FCSTD DOCUMENT  (FreeCAD 1.0R39109 (Git))
Label: XY-Assembly
License: All rights reserved
LicenseURL: https://en.wikipedia.org/wiki/All_rights_reserved
objects: App::FeaturePython×23, App::Link×20, Assembly::AssemblyLink×6, Assembly::JointGroup×1, Assembly::AssemblyObject×1
EXTERNAL_REF file=../Profiles/20x20-I-Type-356mm.FCStd obj=Fusion001
EXTERNAL_REF file=../LinearGuides/MGN12-Rail-300mm.FCStd obj=Part__Feature
EXTERNAL_REF file=SingleCrossCarriageAssembly.FCStd obj=Assembly
EXTERNAL_REF file=SingleCrossCarriageAssembly.FCStd obj=Assembly001
EXTERNAL_REF file=CarriageLinearGuideAssembly.FCStd obj=Body
EXTERNAL_REF file=CarriageLinearGuideAssembly.FCStd obj=Vagon_MGN_021
EXTERNAL_REF file=SingleCrossCarriageAssembly.FCStd obj=Assembly002
EXTERNAL_REF file=SingleCrossCarriageAssembly.FCStd obj=Cube
EXTERNAL_REF file=SingleCrossCarriageAssembly.FCStd obj=Body002

FEATURE [App::Link] Profile_20x20_I_Type_Slot5  label="Profile-20x20-I-Type_Slot5"
  LinkPlacement = pos=(0,-178,178) rot=(1,0,0;4.71239rad)
  LinkedObject = -> <external ../Profiles/20x20-I-Type-356mm.FCStd>#Fusion001
  Placement = pos=(0,-178,178) rot=(1,0,0;4.71239rad)
FEATURE [App::FeaturePython] GroundedJoint  # Assembly grounded joint (typed FeaturePython)
  ObjectToGround = -> Profile_20x20_I_Type_Slot5
  Placement = pos=(0,-178,178) rot=(1,0,0;4.71239rad)
FEATURE [App::Link] Profile_20x20_I_Type_Slot006  label="Profile-20x20-I-Type_Slot006"
  LinkPlacement = pos=(10,-188,180.494) rot=(0,1,0;1.5708rad)
  LinkedObject = -> <external ../Profiles/20x20-I-Type-356mm.FCStd>#Fusion001
  Placement = pos=(10,-188,180.494) rot=(0,1,0;1.5708rad)
FEATURE [App::Link] Profile_20x20_I_Type_Slot007  label="Profile-20x20-I-Type_Slot007"
  LinkPlacement = pos=(10,188,180.494) rot=(0,1,0;1.5708rad)
  LinkedObject = -> <external ../Profiles/20x20-I-Type-356mm.FCStd>#Fusion001
  Placement = pos=(10,188,180.494) rot=(0,1,0;1.5708rad)
FEATURE [App::Link] Profile_20x20_I_Type_Slot008  label="Profile-20x20-I-Type_Slot008"
  LinkPlacement = pos=(376,178,178) rot=(-0.57735,-0.57735,0.57735;4.18879rad)
  LinkedObject = -> <external ../Profiles/20x20-I-Type-356mm.FCStd>#Fusion001
  Placement = pos=(376,178,178) rot=(-0.57735,-0.57735,0.57735;4.18879rad)
FEATURE [App::FeaturePython] Joint  label="Distance"  # Assembly joint (typed FeaturePython)
  Activated = true
  AngleMax = 0
  AngleMin = 0
  Detach1 = false
  Detach2 = false
  Distance = 0
  Distance2 = 0
  EnableAngleMax = false
  EnableAngleMin = false
  EnableLengthMax = false
  EnableLengthMin = false
  JointType = 5 (Distance)
  LengthMax = 0
  LengthMin = 0
  Placement1 = pos=(-5.81322,5.81322,0) rot=(0,0,1;0rad)
  Placement2 = pos=(10,-5.97447,178) rot=(0.57735,0.57735,-0.57735;4.18879rad)
  Reference1 = -> Assembly [Profile_20x20_I_Type_Slot006.Face33,Profile_20x20_I_Type_Slot006.Edge18]
  Reference2 = -> Assembly [Profile_20x20_I_Type_Slot5.Face21,Profile_20x20_I_Type_Slot5.Face21]
FEATURE [App::FeaturePython] Joint001  label="Distance001"  # Assembly joint (typed FeaturePython)
  Activated = true
  AngleMax = 0
  AngleMin = 0
  Detach1 = false
  Detach2 = false
  Distance = 0
  Distance2 = 0
  EnableAngleMax = false
  EnableAngleMin = false
  EnableLengthMax = false
  EnableLengthMin = false
  JointType = 5 (Distance)
  LengthMax = 0
  LengthMin = 0
  Placement1 = pos=(-5.81322,-5.81322,0) rot=(-1,0,0;3.14159rad)
  Placement2 = pos=(-5.97447,10,178) rot=(-1,0,0;1.5708rad)
  Reference1 = -> Assembly [Profile_20x20_I_Type_Slot5.Face10,Profile_20x20_I_Type_Slot5.Edge18]
  Reference2 = -> Assembly [Profile_20x20_I_Type_Slot006.Face85,Profile_20x20_I_Type_Slot006.Vertex140]
FEATURE [App::FeaturePython] Joint002  label="Distance002"  # Assembly joint (typed FeaturePython)
  Activated = true
  AngleMax = 0
  AngleMin = 0
  Detach1 = false
  Detach2 = false
  Distance = 0
  Distance2 = 0
  EnableAngleMax = false
  EnableAngleMin = false
  EnableLengthMax = false
  EnableLengthMin = false
  JointType = 5 (Distance)
  LengthMax = 0
  LengthMin = 0
  Placement1 = pos=(10,-5.97447,178) rot=(0.57735,0.57735,-0.57735;4.18879rad)
  Placement2 = pos=(-5.81322,-5.81322,0) rot=(1,0,0;3.14159rad)
  Reference1 = -> Assembly [Profile_20x20_I_Type_Slot5.Face21,Profile_20x20_I_Type_Slot5.Vertex41]
  Reference2 = -> Assembly [Profile_20x20_I_Type_Slot007.Face10,Profile_20x20_I_Type_Slot007.Vertex61]
FEATURE [App::FeaturePython] Joint003  label="Distance003"  # Assembly joint (typed FeaturePython)
  Activated = true
  AngleMax = 0
  AngleMin = 0
  Detach1 = false
  Detach2 = false
  Distance = 0
  Distance2 = 0
  EnableAngleMax = false
  EnableAngleMin = false
  EnableLengthMax = false
  EnableLengthMin = false
  JointType = 5 (Distance)
  LengthMax = 0
  LengthMin = 0
  Placement1 = pos=(5.81322,-5.81322,356) rot=(0,0,-1;3.14159rad)
  Placement2 = pos=(-5.97447,-10,178) rot=(-1,0,0;1.5708rad)
  Reference1 = -> Assembly [Profile_20x20_I_Type_Slot5.Face5,Profile_20x20_I_Type_Slot5.Edge18]
  Reference2 = -> Assembly [Profile_20x20_I_Type_Slot007.Face44,Profile_20x20_I_Type_Slot007.Vertex61]
FEATURE [App::FeaturePython] Joint004  label="Distance004"  # Assembly joint (typed FeaturePython)
  Activated = true
  AngleMax = 0
  AngleMin = 0
  Detach1 = false
  Detach2 = false
  Distance = 0
  Distance2 = 0
  EnableAngleMax = false
  EnableAngleMin = false
  EnableLengthMax = false
  EnableLengthMin = false
  JointType = 5 (Distance)
  LengthMax = 0
  LengthMin = 0
  Placement1 = pos=(-5.97447,10,178) rot=(-1,0,0;1.5708rad)
  Placement2 = pos=(-5.81322,-5.81322,356) rot=(1,0,0;3.14159rad)
  Reference1 = -> Assembly [Profile_20x20_I_Type_Slot006.Face85,Profile_20x20_I_Type_Slot006.Vertex157]
  Reference2 = -> Assembly [Profile_20x20_I_Type_Slot008.Face25,Profile_20x20_I_Type_Slot008.Edge18]
FEATURE [App::FeaturePython] Joint005  label="Distance005"  # Assembly joint (typed FeaturePython)
  Activated = true
  AngleMax = 0
  AngleMin = 0
  Detach1 = false
  Detach2 = false
  Distance = 0
  Distance2 = 0
  EnableAngleMax = false
  EnableAngleMin = false
  EnableLengthMax = false
  EnableLengthMin = false
  JointType = 5 (Distance)
  LengthMax = 0
  LengthMin = 0
  Placement1 = pos=(-5.81322,5.81322,356) rot=(0,0,1;0rad)
  Placement2 = pos=(-5.97447,-10,178) rot=(-1,0,0;1.5708rad)
  Reference1 = -> Assembly [Profile_20x20_I_Type_Slot006.Face68,Profile_20x20_I_Type_Slot006.Vertex151]
  Reference2 = -> Assembly [Profile_20x20_I_Type_Slot008.Face44,Profile_20x20_I_Type_Slot008.Vertex101]
FEATURE [App::FeaturePython] Joint006  label="Distance006"  # Assembly joint (typed FeaturePython)
  Activated = true
  AngleMax = 0
  AngleMin = 0
  Detach1 = false
  Detach2 = false
  Distance = 0
  Distance2 = 0
  EnableAngleMax = false
  EnableAngleMin = false
  EnableLengthMax = false
  EnableLengthMin = false
  JointType = 5 (Distance)
  LengthMax = 0
  LengthMin = 0
  Placement1 = pos=(5.97447,-10,178) rot=(0,0.707107,-0.707107;3.14159rad)
  Placement2 = pos=(-10,-5.97447,178) rot=(-0.57735,-0.57735,0.57735;2.0944rad)
  Reference1 = -> Assembly [Profile_20x20_I_Type_Slot5.Face23,Profile_20x20_I_Type_Slot5.Vertex43]
  Reference2 = -> Assembly [Profile_20x20_I_Type_Slot008.Face42,Profile_20x20_I_Type_Slot008.Face42]
FEATURE [App::FeaturePython] Joint007  label="Distance007"  # Assembly joint (typed FeaturePython)
  Activated = true
  AngleMax = 0
  AngleMin = 0
  Detach1 = false
  Detach2 = false
  Distance = 0
  Distance2 = 0
  EnableAngleMax = false
  EnableAngleMin = false
  EnableLengthMax = false
  EnableLengthMin = false
  JointType = 5 (Distance)
  LengthMax = 0
  LengthMin = 0
  Placement1 = pos=(-10,-5.97447,178) rot=(-0.57735,-0.57735,0.57735;2.0944rad)
  Placement2 = pos=(-10,5.97447,178) rot=(-0.57735,0.57735,-0.57735;2.0944rad)
  Reference1 = -> Assembly [Profile_20x20_I_Type_Slot007.Face42,Profile_20x20_I_Type_Slot007.Face42]
  Reference2 = -> Assembly [Profile_20x20_I_Type_Slot006.Face83,Profile_20x20_I_Type_Slot006.Face83]
FEATURE [App::Link] Rail_12  label="Rail 12"
  LinkPlacement = pos=(13.95,-150,178) rot=(0,-1,0;1.5708rad)
  LinkedObject = -> <external ../LinearGuides/MGN12-Rail-300mm.FCStd>#Part__Feature
  Placement = pos=(13.95,-150,178) rot=(0,-1,0;1.5708rad)
FEATURE [App::Link] Rail_013  label="Rail 013"
  LinkPlacement = pos=(362.05,150,178) rot=(0.707107,0,0.707107;3.14159rad)
  LinkedObject = -> <external ../LinearGuides/MGN12-Rail-300mm.FCStd>#Part__Feature
  Placement = pos=(362.05,150,178) rot=(0.707107,0,0.707107;3.14159rad)
FEATURE [App::Link] Rail_014  label="Rail 014"
  LinkPlacement = pos=(338,-174.05,180.494) rot=(0.57735,-0.57735,0.57735;2.0944rad)
  LinkedObject = -> <external ../LinearGuides/MGN12-Rail-300mm.FCStd>#Part__Feature
  Placement = pos=(338,-174.05,180.494) rot=(0.57735,-0.57735,0.57735;2.0944rad)
FEATURE [App::Link] Rail_015  label="Rail 015"
  LinkPlacement = pos=(38,174.05,180.494) rot=(0.57735,0.57735,0.57735;4.18879rad)
  LinkedObject = -> <external ../LinearGuides/MGN12-Rail-300mm.FCStd>#Part__Feature
  Placement = pos=(38,174.05,180.494) rot=(0.57735,0.57735,0.57735;4.18879rad)
FEATURE [App::FeaturePython] Joint008  label="Distance008"  # Assembly joint (typed FeaturePython)
  Activated = true
  AngleMax = 0
  AngleMin = 0
  Detach1 = false
  Detach2 = false
  Distance = 0
  Distance2 = 0
  EnableAngleMax = false
  EnableAngleMin = false
  EnableLengthMax = false
  EnableLengthMin = false
  JointType = 5 (Distance)
  LengthMax = 0
  LengthMin = 0
  Placement1 = pos=(1.30928,149.976,3.95) rot=(0,1,0;3.14159rad)
  Placement2 = pos=(10,-5.97447,178) rot=(0.57735,0.57735,-0.57735;4.18879rad)
  Reference1 = -> Assembly [Rail_12.Face37,Rail_12.Vertex52]
  Reference2 = -> Assembly [Profile_20x20_I_Type_Slot5.Face21,Profile_20x20_I_Type_Slot5.Vertex23]
FEATURE [App::FeaturePython] Joint009  label="Distance009"  # Assembly joint (typed FeaturePython)
  Activated = true
  AngleMax = 0
  AngleMin = 0
  Detach1 = false
  Detach2 = false
  Distance = 0
  Distance2 = 0
  EnableAngleMax = false
  EnableAngleMin = false
  EnableLengthMax = false
  EnableLengthMin = false
  JointType = 5 (Distance)
  LengthMax = 0
  LengthMin = 0
  Placement1 = pos=(1.30928,149.976,3.95) rot=(0,-1,0;3.14159rad)
  Placement2 = pos=(-5.97447,-10,178) rot=(-1,0,0;1.5708rad)
  Reference1 = -> Assembly [Rail_013.Face37,Rail_013.Vertex64]
  Reference2 = -> Assembly [Profile_20x20_I_Type_Slot008.Face44,Profile_20x20_I_Type_Slot008.Face44]
FEATURE [App::FeaturePython] Joint010  label="Distance010"  # Assembly joint (typed FeaturePython)
  Activated = true
  AngleMax = 0
  AngleMin = 0
  Detach1 = false
  Detach2 = false
  Distance = 0
  Distance2 = 0
  EnableAngleMax = false
  EnableAngleMin = false
  EnableLengthMax = false
  EnableLengthMin = false
  JointType = 5 (Distance)
  LengthMax = 0
  LengthMin = 0
  Placement1 = pos=(1.30928,149.976,3.95) rot=(0,-1,0;3.14159rad)
  Placement2 = pos=(-5.97447,-10,178) rot=(-1,0,0;1.5708rad)
  Reference1 = -> Assembly [Rail_015.Face37,Rail_015.Edge19]
  Reference2 = -> Assembly [Profile_20x20_I_Type_Slot007.Face44,Profile_20x20_I_Type_Slot007.Face44]
FEATURE [App::FeaturePython] Joint011  label="Distance011"  # Assembly joint (typed FeaturePython)
  Activated = true
  AngleMax = 0
  AngleMin = 0
  Detach1 = false
  Detach2 = false
  Distance = 0
  Distance2 = 0
  EnableAngleMax = false
  EnableAngleMin = false
  EnableLengthMax = false
  EnableLengthMin = false
  JointType = 5 (Distance)
  LengthMax = 0
  LengthMin = 0
  Placement1 = pos=(1.30928,149.976,3.95) rot=(0,-1,0;3.14159rad)
  Placement2 = pos=(-5.97447,10,178) rot=(-1,0,0;1.5708rad)
  Reference1 = -> Assembly [Rail_014.Face37,Rail_014.Edge17]
  Reference2 = -> Assembly [Profile_20x20_I_Type_Slot006.Face85,Profile_20x20_I_Type_Slot006.Vertex157]
FEATURE [App::FeaturePython] Joint012  label="Distance012"  # Assembly joint (typed FeaturePython)
  Activated = true
  AngleMax = 0
  AngleMin = 0
  Detach1 = false
  Detach2 = false
  Distance = -4
  Distance2 = 0
  EnableAngleMax = false
  EnableAngleMin = false
  EnableLengthMax = false
  EnableLengthMin = false
  JointType = 5 (Distance)
  LengthMax = 0
  LengthMin = 0
  Placement1 = pos=(-10,-5.97447,178) rot=(-0.57735,-0.57735,0.57735;2.0944rad)
  Placement2 = pos=(6,150,1.25) rot=(0,-1,0;1.5708rad)
  Reference1 = -> Assembly [Profile_20x20_I_Type_Slot008.Face42,Profile_20x20_I_Type_Slot008.Face42]
  Reference2 = -> Assembly [Rail_013.Face49,Rail_013.Face49]
FEATURE [App::FeaturePython] Joint013  label="Distance013"  # Assembly joint (typed FeaturePython)
  Activated = true
  AngleMax = 0
  AngleMin = 0
  Detach1 = false
  Detach2 = false
  Distance = -4
  Distance2 = 0
  EnableAngleMax = false
  EnableAngleMin = false
  EnableLengthMax = false
  EnableLengthMin = false
  JointType = 5 (Distance)
  LengthMax = 0
  LengthMin = 0
  Placement1 = pos=(6,150,1.25) rot=(0,-1,0;1.5708rad)
  Placement2 = pos=(-10,-5.97447,178) rot=(-0.57735,-0.57735,0.57735;2.0944rad)
  Reference1 = -> Assembly [Rail_015.Face49,Rail_015.Face49]
  Reference2 = -> Assembly [Profile_20x20_I_Type_Slot007.Face42,Profile_20x20_I_Type_Slot007.Face42]
FEATURE [App::FeaturePython] Joint014  label="Distance014"  # Assembly joint (typed FeaturePython)
  Activated = true
  AngleMax = 0
  AngleMin = 0
  Detach1 = false
  Detach2 = false
  Distance = -4
  Distance2 = 0
  EnableAngleMax = false
  EnableAngleMin = false
  EnableLengthMax = false
  EnableLengthMin = false
  JointType = 5 (Distance)
  LengthMax = 0
  LengthMin = 0
  Placement1 = pos=(5.97447,-10,178) rot=(0,0.707107,-0.707107;3.14159rad)
  Placement2 = pos=(6,150,1.25) rot=(0,1,0;4.71239rad)
  Reference1 = -> Assembly [Profile_20x20_I_Type_Slot5.Face23,Profile_20x20_I_Type_Slot5.Vertex43]
  Reference2 = -> Assembly [Rail_12.Face49,Rail_12.Face49]
FEATURE [App::FeaturePython] Joint015  label="Distance015"  # Assembly joint (typed FeaturePython)
  Activated = true
  AngleMax = 0
  AngleMin = 0
  Detach1 = false
  Detach2 = false
  Distance = -4
  Distance2 = 0
  EnableAngleMax = false
  EnableAngleMin = false
  EnableLengthMax = false
  EnableLengthMin = false
  JointType = 5 (Distance)
  LengthMax = 0
  LengthMin = 0
  Placement1 = pos=(6,150,1.25) rot=(0,1,0;4.71239rad)
  Placement2 = pos=(-10,5.97447,178) rot=(-0.57735,0.57735,-0.57735;2.0944rad)
  Reference1 = -> Assembly [Rail_014.Face49,Rail_014.Vertex101]
  Reference2 = -> Assembly [Profile_20x20_I_Type_Slot006.Face83,Profile_20x20_I_Type_Slot006.Vertex138]
FEATURE [App::FeaturePython] Joint016  label="Distance016"  # Assembly joint (typed FeaturePython)
  Activated = true
  AngleMax = 0
  AngleMin = 0
  Detach1 = false
  Detach2 = false
  Distance = 28
  Distance2 = 0
  EnableAngleMax = false
  EnableAngleMin = false
  EnableLengthMax = false
  EnableLengthMin = false
  JointType = 5 (Distance)
  LengthMax = 0
  LengthMin = 0
  Placement1 = pos=(0.00361996,300,0.103497) rot=(-0.57735,-0.57735,-0.57735;2.0944rad)
  Placement2 = pos=(-5.81322,5.81322,356) rot=(0,0,1;0rad)
  Reference1 = -> Assembly [Rail_015.Face38,Rail_015.Vertex104]
  Reference2 = -> Assembly [Profile_20x20_I_Type_Slot007.Face68,Profile_20x20_I_Type_Slot007.Edge18]
FEATURE [App::FeaturePython] Joint017  label="Distance017"  # Assembly joint (typed FeaturePython)
  Activated = true
  AngleMax = 0
  AngleMin = 0
  Detach1 = false
  Detach2 = false
  Distance = 0
  Distance2 = 0
  EnableAngleMax = false
  EnableAngleMin = false
  EnableLengthMax = false
  EnableLengthMin = false
  JointType = 5 (Distance)
  LengthMax = 0
  LengthMin = 0
  Placement1 = pos=(0.00361996,0,0.103497) rot=(-0.57735,-0.57735,-0.57735;2.0944rad)
  Placement2 = pos=(0.00361996,300,0.103497) rot=(-0.57735,-0.57735,-0.57735;2.0944rad)
  Reference1 = -> Assembly [Rail_014.Face39,Rail_014.Vertex135]
  Reference2 = -> Assembly [Rail_015.Face38,Rail_015.Vertex118]
FEATURE [App::FeaturePython] Joint018  label="Distance018"  # Assembly joint (typed FeaturePython)
  Activated = true
  AngleMax = 0
  AngleMin = 0
  Detach1 = false
  Detach2 = false
  Distance = -28
  Distance2 = 0
  EnableAngleMax = false
  EnableAngleMin = false
  EnableLengthMax = false
  EnableLengthMin = false
  JointType = 5 (Distance)
  LengthMax = 0
  LengthMin = 0
  Placement1 = pos=(0.00361996,-2.84e-14,0.103497) rot=(-0.57735,-0.57735,-0.57735;2.0944rad)
  Placement2 = pos=(-5.81322,-5.81322,0) rot=(1,0,0;3.14159rad)
  Reference1 = -> Assembly [Rail_013.Face39,Rail_013.Vertex128]
  Reference2 = -> Assembly [Profile_20x20_I_Type_Slot008.Face10,Profile_20x20_I_Type_Slot008.Vertex46]
FEATURE [App::FeaturePython] Joint019  label="Distance019"  # Assembly joint (typed FeaturePython)
  Activated = true
  AngleMax = 0
  AngleMin = 0
  Detach1 = false
  Detach2 = false
  Distance = 0
  Distance2 = 0
  EnableAngleMax = false
  EnableAngleMin = false
  EnableLengthMax = false
  EnableLengthMin = false
  JointType = 5 (Distance)
  LengthMax = 0
  LengthMin = 0
  Placement1 = pos=(0.00361996,-2.84e-14,0.103497) rot=(-0.57735,-0.57735,-0.57735;2.0944rad)
  Placement2 = pos=(0.00361996,300,0.103497) rot=(0.57735,0.57735,0.57735;4.18879rad)
  Reference1 = -> Assembly [Rail_013.Face39,Rail_013.Face39]
  Reference2 = -> Assembly [Rail_12.Face38,Rail_12.Vertex118]
FEATURE [App::Link] Body
  LinkedObject = -> <external CarriageLinearGuideAssembly.FCStd>#Body
FEATURE [App::Link] Vagon_MGN_021  label="Vagon MGN 021"
  LinkPlacement = pos=(165.94,286.797,-72.844) rot=(0.57735,-0.57735,0.57735;2.0944rad)
  LinkedObject = -> <external CarriageLinearGuideAssembly.FCStd>#Vagon_MGN_021
  Placement = pos=(165.94,286.797,-72.844) rot=(0.57735,-0.57735,0.57735;2.0944rad)
FEATURE [Assembly::AssemblyLink] Assembly002
  Group = -> [Body,Vagon_MGN_021]
  LinkedObject = -> <external SingleCrossCarriageAssembly.FCStd>#Assembly001
  Rigid = true
FEATURE [App::Link] Body001
  LinkedObject = -> <external CarriageLinearGuideAssembly.FCStd>#Body
FEATURE [App::Link] Vagon_MGN_022  label="Vagon MGN 022"
  LinkPlacement = pos=(165.94,286.797,-72.844) rot=(0.57735,-0.57735,0.57735;2.0944rad)
  LinkedObject = -> <external CarriageLinearGuideAssembly.FCStd>#Vagon_MGN_021
  Placement = pos=(165.94,286.797,-72.844) rot=(0.57735,-0.57735,0.57735;2.0944rad)
FEATURE [Assembly::AssemblyLink] Assembly003
  Group = -> [Body001,Vagon_MGN_022]
  LinkedObject = -> <external SingleCrossCarriageAssembly.FCStd>#Assembly002
  Placement = pos=(55,299.5,-1.21e-14) rot=(0,0,1;3.14159rad)
  Rigid = true
FEATURE [App::Link] Cube
  LinkPlacement = pos=(32.5,314.75,8.5) rot=(0,0,1;3.14159rad)
  LinkedObject = -> <external SingleCrossCarriageAssembly.FCStd>#Cube
  Placement = pos=(32.5,314.75,8.5) rot=(0,0,1;3.14159rad)
FEATURE [App::Link] Body002
  LinkPlacement = pos=(32.5,149.5,13.5) rot=(0.57735,0.57735,-0.57735;2.0944rad)
  LinkedObject = -> <external SingleCrossCarriageAssembly.FCStd>#Body002
  Placement = pos=(32.5,149.5,13.5) rot=(0.57735,0.57735,-0.57735;2.0944rad)
FEATURE [Assembly::AssemblyLink] Assembly001
  Group = -> [Assembly002,Assembly003,Cube,Body002]
  LinkedObject = -> <external SingleCrossCarriageAssembly.FCStd>#Assembly
  Origin = -> Origin001
  Rigid = true
FEATURE [App::Link] Body003
  LinkedObject = -> <external CarriageLinearGuideAssembly.FCStd>#Body
FEATURE [App::Link] Vagon_MGN_023  label="Vagon MGN 023"
  LinkPlacement = pos=(165.94,286.797,-72.844) rot=(0.57735,-0.57735,0.57735;2.0944rad)
  LinkedObject = -> <external CarriageLinearGuideAssembly.FCStd>#Vagon_MGN_021
  Placement = pos=(165.94,286.797,-72.844) rot=(0.57735,-0.57735,0.57735;2.0944rad)
FEATURE [Assembly::AssemblyLink] Assembly005
  Group = -> [Body003,Vagon_MGN_023]
  LinkedObject = -> <external SingleCrossCarriageAssembly.FCStd>#Assembly001
  Rigid = true
FEATURE [App::Link] Body004
  LinkedObject = -> <external CarriageLinearGuideAssembly.FCStd>#Body
FEATURE [App::Link] Vagon_MGN_024  label="Vagon MGN 024"
  LinkPlacement = pos=(165.94,286.797,-72.844) rot=(0.57735,-0.57735,0.57735;2.0944rad)
  LinkedObject = -> <external CarriageLinearGuideAssembly.FCStd>#Vagon_MGN_021
  Placement = pos=(165.94,286.797,-72.844) rot=(0.57735,-0.57735,0.57735;2.0944rad)
FEATURE [Assembly::AssemblyLink] Assembly006
  Group = -> [Body004,Vagon_MGN_024]
  LinkedObject = -> <external SingleCrossCarriageAssembly.FCStd>#Assembly002
  Placement = pos=(55,299.5,-1.21e-14) rot=(0,0,1;3.14159rad)
  Rigid = true
FEATURE [App::Link] Cube001
  LinkPlacement = pos=(32.5,314.75,8.5) rot=(0,0,1;3.14159rad)
  LinkedObject = -> <external SingleCrossCarriageAssembly.FCStd>#Cube
  Placement = pos=(32.5,314.75,8.5) rot=(0,0,1;3.14159rad)
FEATURE [App::Link] Body005
  LinkPlacement = pos=(32.5,149.5,13.5) rot=(0.57735,0.57735,-0.57735;2.0944rad)
  LinkedObject = -> <external SingleCrossCarriageAssembly.FCStd>#Body002
  Placement = pos=(32.5,149.5,13.5) rot=(0.57735,0.57735,-0.57735;2.0944rad)
FEATURE [Assembly::AssemblyLink] Assembly004
  Group = -> [Assembly005,Assembly006,Cube001,Body005]
  LinkedObject = -> <external SingleCrossCarriageAssembly.FCStd>#Assembly
  Origin = -> Origin002
  Placement = pos=(38,32.9248,164.5) rot=(0,0,-1;1.5708rad)
  Rigid = true
FEATURE [App::FeaturePython] Joint020  label="Distance020"  # Assembly joint (typed FeaturePython)
  Activated = true
  AngleMax = 0
  AngleMin = 0
  Detach1 = false
  Detach2 = false
  Distance = -0.1
  Distance2 = 0
  EnableAngleMax = false
  EnableAngleMin = false
  EnableLengthMax = false
  EnableLengthMin = false
  JointType = 5 (Distance)
  LengthMax = 0
  LengthMin = 0
  Placement1 = pos=(-6,150,1.25) rot=(0,1,0;4.71239rad)
  Placement2 = pos=(80.444,138.44,310.568) rot=(0.57735,0.57735,0.57735;2.0944rad)
  Reference1 = -> Assembly [Rail_12.Face47,Rail_12.Face47]
  Reference2 = -> Assembly [Assembly004.Assembly005.Vagon_MGN_023.Part__Feature006.Face24,Assembly004.Assembly005.Vagon_MGN_023.Part__Feature006.Face24]
FEATURE [App::FeaturePython] Joint021  label="Distance021"  # Assembly joint (typed FeaturePython)
  Activated = true
  AngleMax = 0
  AngleMin = 0
  Detach1 = false
  Detach2 = false
  Distance = 0.25
  Distance2 = 0
  EnableAngleMax = false
  EnableAngleMin = false
  EnableLengthMax = false
  EnableLengthMin = false
  JointType = 5 (Distance)
  LengthMax = 0
  LengthMin = 0
  Placement1 = pos=(86.344,138.44,306.647) rot=(0,0,1;0rad)
  Placement2 = pos=(1.705e-13,149.943,-3.95) rot=(0,1,0;3.14159rad)
  Reference1 = -> Assembly [Assembly004.Assembly005.Vagon_MGN_023.Part__Feature006.Face32,Assembly004.Assembly005.Vagon_MGN_023.Part__Feature006.Vertex24]
  Reference2 = -> Assembly [Rail_12.Face42,Rail_12.Edge15]
FEATURE [Assembly::JointGroup] Joints
  Group = -> [GroundedJoint,Joint,Joint001,Joint002,Joint003,Joint004,Joint005,Joint006,Joint007,Joint008,Joint009,Joint010,Joint011,Joint012,Joint013,Joint014,Joint015,Joint016,Joint017,Joint018,Joint019,Joint020,Joint021]
FEATURE [Assembly::AssemblyObject] Assembly
  Group = -> [Joints,Profile_20x20_I_Type_Slot5,GroundedJoint,Profile_20x20_I_Type_Slot006,Profile_20x20_I_Type_Slot007,Profile_20x20_I_Type_Slot008,Joint,Joint001,Joint002,Joint003,Joint004,Joint005,Joint006,Joint007,Rail_12,Rail_013,Rail_014,Rail_015,Joint008,Joint009,Joint010,Joint011,Joint012,Joint013,Joint014,Joint015,Joint016,Joint017,Joint018,Joint019,Assembly001,Assembly004,Joint020,Joint021]
  Origin = -> Origin
  Type = Assembly

RESOLVED EXTERNAL PARTS (link-assembly join: the EXTERNAL_REF files above that resolve inside this repo's crawl, each included once):
---- part ../Profiles/20x20-I-Type-356mm.FCStd = doc fcstd_b290ea92aa36 ----
FCSTD DOCUMENT  (FreeCAD 1.0R39109 (Git))
Label: 20x20-I-Type-356mm
License: All rights reserved
LicenseURL: https://en.wikipedia.org/wiki/All_rights_reserved
objects: Part::Mirroring×2, Part::MultiFuse×2, Sketcher::SketchObject×1, PartDesign::Pad×1, PartDesign::Body×1
note: 10 computed .brp shape members not serialized (recipe doc carries the construction recipe); baked Part::Feature solids carry a one-line shape summary decoded from their .brp

FEATURE [Sketcher::SketchObject] Sketch
  ArcFitTolerance = 0
  AttachmentSupport = -> [XY_Plane]
  FullyConstrained = true
  MakeInternals = false
  MapMode = 5
  sketch-geometry (22):
    g0: ArcOfCircle CenterX=0 CenterY=0 CenterZ=0 NormalX=0 NormalY=0 NormalZ=1 AngleXU=0 Radius=2.15 StartAngle=1.5708 EndAngle=3.14159
    g1: LineSegment StartX=-8.28947 StartY=10 StartZ=0 EndX=-3.65947 EndY=10 EndZ=0
    g2: LineSegment StartX=-2.85947 StartY=9.2 StartZ=0 EndX=-2.85947 EndY=8.5 EndZ=0
    g3: LineSegment StartX=-3.15947 StartY=8.2 StartZ=0 EndX=-5.32947 EndY=8.2 EndZ=0
    g4: LineSegment StartX=-5.8555 StartY=6.87 StartZ=0 EndX=-3.36 EndY=4.53 EndZ=0
    g5: LineSegment StartX=-1.135 StartY=3.65 StartZ=0 EndX=2e-16 EndY=3.65 EndZ=0
    g6: LineSegment StartX=1e-16 StartY=3.65 StartZ=0 EndX=1e-16 EndY=2.15 EndZ=0
    g7: LineSegment StartX=-10 StartY=8.28947 StartZ=0 EndX=-10 EndY=3.65947 EndZ=0
    g8: LineSegment StartX=-9.2 StartY=2.85947 StartZ=0 EndX=-8.5 EndY=2.85947 EndZ=0
    g9: LineSegment StartX=-8.2 StartY=3.15947 StartZ=0 EndX=-8.2 EndY=5.32947 EndZ=0
    g10: LineSegment StartX=-6.87 StartY=5.8555 StartZ=0 EndX=-4.53 EndY=3.36 EndZ=0
    g11: ArcOfCircle CenterX=-8.28947 CenterY=8.28947 CenterZ=0 NormalX=0 NormalY=0 NormalZ=1 AngleXU=0 Radius=1.71053 StartAngle=1.5708 EndAngle=3.14159
    g12: ArcOfCircle CenterX=-9.2 CenterY=3.65947 CenterZ=0 NormalX=0 NormalY=0 NormalZ=1 AngleXU=0 Radius=0.8 StartAngle=3.14159 EndAngle=4.71239
    g13: ArcOfCircle CenterX=-8.5 CenterY=3.15947 CenterZ=0 NormalX=0 NormalY=0 NormalZ=1 AngleXU=0 Radius=0.3 StartAngle=4.71239 EndAngle=6.28319
    g14: ArcOfCircle CenterX=-7.43098 CenterY=5.32947 CenterZ=0 NormalX=0 NormalY=0 NormalZ=1 AngleXU=0 Radius=0.769022 StartAngle=0.753252 EndAngle=3.14159
    g15: ArcOfCircle CenterX=-1.135 CenterY=6.90286 CenterZ=0 NormalX=0 NormalY=0 NormalZ=1 AngleXU=0 Radius=3.25286 StartAngle=3.95914 EndAngle=4.71239
    g16: ArcOfCircle CenterX=-5.32947 CenterY=7.43098 CenterZ=0 NormalX=0 NormalY=0 NormalZ=1 AngleXU=0 Radius=0.769022 StartAngle=1.5708 EndAngle=3.95914
    g17: ArcOfCircle CenterX=-3.15947 CenterY=8.5 CenterZ=0 NormalX=0 NormalY=0 NormalZ=1 AngleXU=0 Radius=0.3 StartAngle=4.71239 EndAngle=6.28319
    g18: ArcOfCircle CenterX=-3.65947 CenterY=9.2 CenterZ=0 NormalX=0 NormalY=0 NormalZ=1 AngleXU=0 Radius=0.8 StartAngle=4e-16 EndAngle=1.5708
    g19: LineSegment StartX=-3.65 StartY=1.135 StartZ=0 EndX=-3.65 EndY=2e-16 EndZ=0
    g20: LineSegment StartX=-3.65 StartY=2e-16 StartZ=0 EndX=-2.15 EndY=2e-16 EndZ=0
    g21: ArcOfCircle CenterX=-6.90286 CenterY=1.135 CenterZ=0 NormalX=0 NormalY=0 NormalZ=1 AngleXU=0 Radius=3.25286 StartAngle=0 EndAngle=0.753252
  constraints (57):
    c: Diameter(g0) = 4.3
    c: Horizontal(g1)
    c: Coincident(g5,g6)
    c: Vertical(g6)
    c: Vertical(g7)
    c: Tangent(g7,g11) = -1.5708
    c: Tangent(g1,g11) = 1.5708
    c: Tangent(g7,g12) = -1.5708
    c: Tangent(g8,g12) = -1.5708
    c: Tangent(g8,g13) = -1.5708
    c: Tangent(g9,g13) = -1.5708
    c: Tangent(g9,g14) = 1.5708
    c: Tangent(g10,g14) = 1.5708
    c: Tangent(g4,g15) = -1.5708
    c: Tangent(g5,g15) = -1.5708
    c: Tangent(g4,g16) = -1.5708
    c: Tangent(g3,g16) = -1.5708
    c: Tangent(g3,g17) = 1.5708
    c: Tangent(g2,g17) = 1.5708
    c: Tangent(g2,g18) = 1.5708
    c: Tangent(g1,g18) = 1.5708
    c: Vertical(g19)
    c: Coincident(g19,g20)
    c: Horizontal(g20)
    c: Tangent(g10,g21) = 1.5708
    c: Tangent(g19,g21) = 1.5708
    c: DistanceY(g6,g6) = 1.5
    c: DistanceX(g20,g20) = 1.5
    c: DistanceY(g0,g20) = 0
    c: DistanceX(g6,g0) = 0
    c: Coincident(g0,g20)
    c: Coincident(g0,g6)
    c: DistanceX(g7,g0) = 10
    c: DistanceY(g0,g1) = 10
    c: Horizontal(g5)
    c: DistanceX(g5,g5) = 1.135
    c: DistanceY(g19,g19) = 1.135
    c: DistanceX(g1,g1) = 4.63
    c: DistanceY(g7,g7) = 4.63
    c: DistanceX(g4,g0) = 3.36
    c: DistanceY(g0,g4) = 2.38
    c: DistanceY(g0,g10) = 3.36
    c: DistanceX(g10,g0) = 2.38
    c: DistanceY(g0,g4) = 4.72
    c: DistanceX(g10,g0) = 4.72
    c: DistanceX(g3,g3) = 2.17
    c: DistanceY(g9,g9) = 2.17
    c: Horizontal(g3)
    c: Vertical(g9)
    c: DistanceY(g3,g1) = 1.8
    c: DistanceX(g7,g9) = 1.8
    c: DistanceY(g3,g2) = 0.3
    c: DistanceX(g1,g2) = 0.8
    c: DistanceY(g2,g1) = 0.8
    c: DistanceY(g8,g9) = 0.3
    c: DistanceY(g8,g7) = 0.8
    c: Coincident(g0,g-1)
FEATURE [PartDesign::Pad] Pad  label="SetLength"
  Direction = (0,0,1)
  Length = 356
  Length2 = 10
  Profile = -> Sketch
  ReferenceAxis = -> Sketch [N_Axis]
  Suppressed = false
  Type = 0
FEATURE [PartDesign::Body] Body
  AllowCompound = false
  Group = -> [Sketch,Pad]
  Origin = -> Origin
  Tip = -> Pad
FEATURE [Part::Mirroring] Part__Mirroring  label="SetLength (Mirror #1)"
  Base = (0,0,0)
  Normal = (0,1,0)
  Source = -> Pad
FEATURE [Part::MultiFuse] Fusion
  Shapes = -> [Part__Mirroring,Pad]
FEATURE [Part::Mirroring] Part__Mirroring001  label="Fusion (Mirror #2)"
  Base = (0,0,0)
  Normal = (1,0,0)
  Source = -> Fusion
FEATURE [Part::MultiFuse] Fusion001  label="Profile-20x20-I-Type_Slot5"
  Shapes = -> [Part__Mirroring001,Fusion]
---- part CarriageLinearGuideAssembly.FCStd = doc fcstd_5ef0b1130dcc ----
FCSTD DOCUMENT  (FreeCAD 1.0R39109 (Git))
Label: CarriageLinearGuideAssembly
License: All rights reserved
LicenseURL: https://en.wikipedia.org/wiki/All_rights_reserved
objects: App::FeaturePython×3, App::Link×2, Assembly::JointGroup×1, Assembly::AssemblyObject×1
EXTERNAL_REF file=CrossCarriage.FCStd obj=Body
EXTERNAL_REF file=../LinearGuides/MGN12H.FCStd obj=Vagon_MGN_12

FEATURE [App::Link] Body
  LinkedObject = -> <external CrossCarriage.FCStd>#Body
FEATURE [App::FeaturePython] GroundedJoint  # Assembly grounded joint (typed FeaturePython)
  ObjectToGround = -> Body
FEATURE [App::Link] Vagon_MGN_021  label="Vagon MGN 021"
  LinkPlacement = pos=(165.94,287.047,-72.844) rot=(0.57735,-0.57735,0.57735;2.0944rad)
  LinkedObject = -> <external ../LinearGuides/MGN12H.FCStd>#Vagon_MGN_12
  Placement = pos=(165.94,287.047,-72.844) rot=(0.57735,-0.57735,0.57735;2.0944rad)
FEATURE [App::FeaturePython] Joint  label="Revolute"  # Assembly joint (typed FeaturePython)
  Activated = true
  AngleMax = 0
  AngleMin = 0
  Detach1 = false
  Detach2 = false
  Distance = 0
  Distance2 = 0
  EnableAngleMax = false
  EnableAngleMin = false
  EnableLengthMax = false
  EnableLengthMin = false
  JointType = 1 (Revolute)
  LengthMax = 0
  LengthMin = 0
  Offset2 = pos=(0,0,-0.25) rot=(0,0,1;0rad)
  Placement1 = pos=(17.5,-15,23.5) rot=(1,0,0;1.5708rad)
  Placement2 = pos=(96.344,148.44,302.047) rot=(0,1,0;3.14159rad)
  Reference1 = -> Assembly [Body.Edge23,Body.Edge23]
  Reference2 = -> Assembly [Vagon_MGN_021.Part__Feature006.Edge232,Vagon_MGN_021.Part__Feature006.Edge232]
FEATURE [App::FeaturePython] Joint001  label="Revolute001"  # Assembly joint (typed FeaturePython)
  Activated = true
  AngleMax = 0
  AngleMin = 0
  Detach1 = false
  Detach2 = false
  Distance = 0
  Distance2 = 0
  EnableAngleMax = false
  EnableAngleMin = false
  EnableLengthMax = false
  EnableLengthMin = false
  JointType = 1 (Revolute)
  LengthMax = 0
  LengthMin = 0
  Offset2 = pos=(0,0,-0.25) rot=(0,0,1;0rad)
  Placement1 = pos=(76.344,128.44,301.797) rot=(0,1,0;3.14159rad)
  Placement2 = pos=(37.5,-14.75,3.5) rot=(1,0,0;1.5708rad)
  Reference1 = -> Assembly [Vagon_MGN_021.Part__Feature006.Edge235,Vagon_MGN_021.Part__Feature006.Edge235]
  Reference2 = -> Assembly [Body.Edge34,Body.Edge34]
FEATURE [Assembly::JointGroup] Joints
  Group = -> [GroundedJoint,Joint,Joint001]
FEATURE [Assembly::AssemblyObject] Assembly
  Group = -> [Joints,Body,GroundedJoint,Vagon_MGN_021,Joint,Joint001]
  Origin = -> Origin
  Type = Assembly
